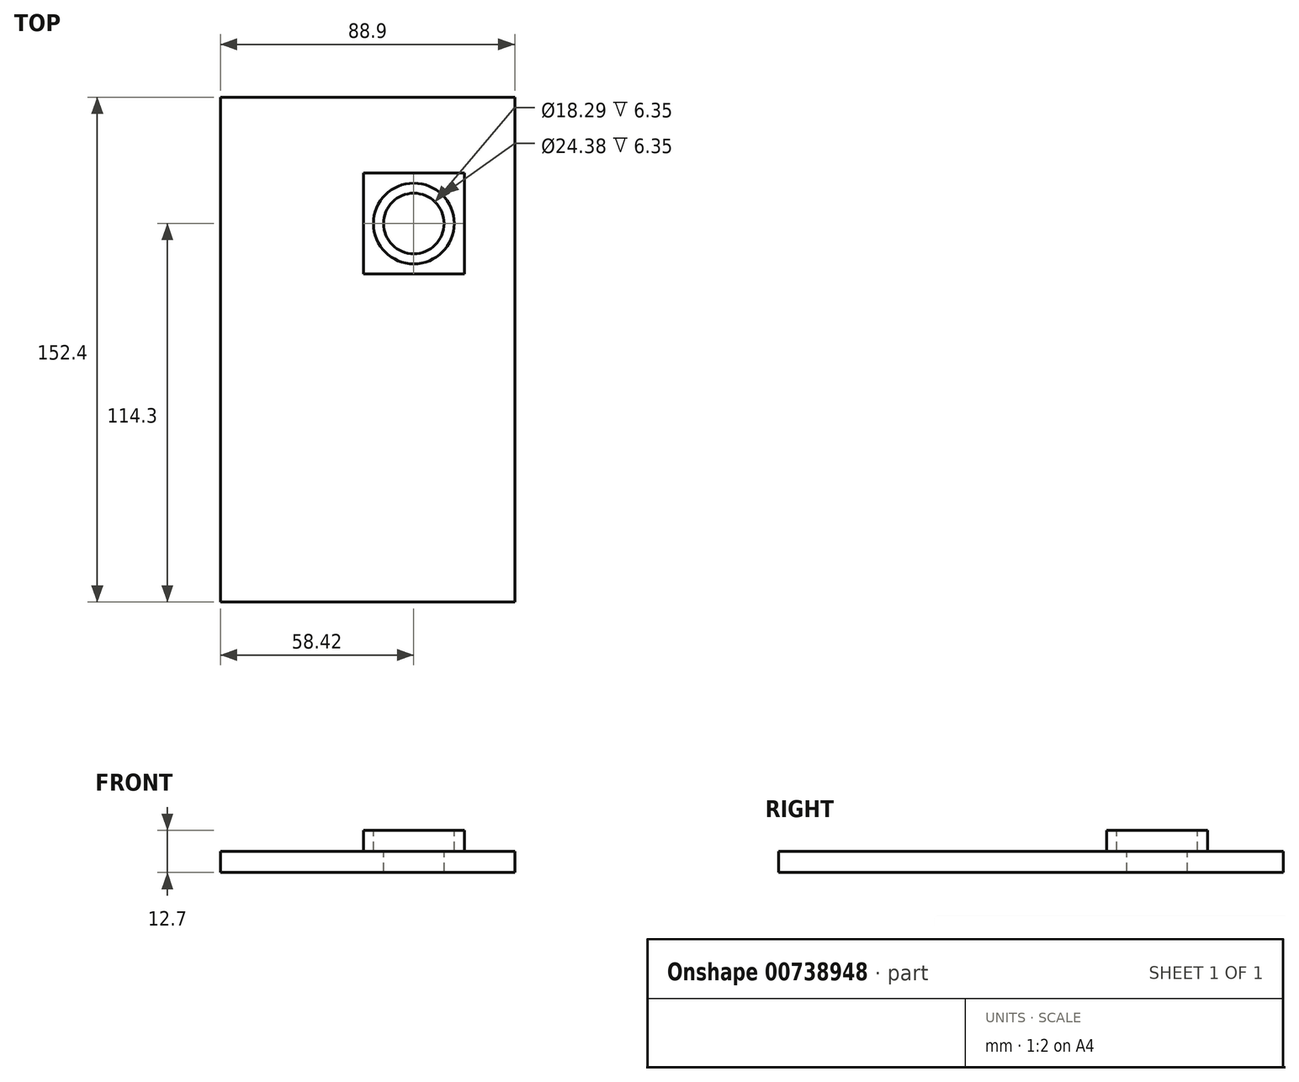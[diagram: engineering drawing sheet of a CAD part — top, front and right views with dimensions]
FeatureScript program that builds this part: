
annotation { "Feature Type Name" : "Feature", "Feature Type Description" : "" }
export const myFeature = defineFeature(function(context is Context, id is Id, definition is map)
    precondition{}
    {
        {
            var Q0;
            Q0=qCreatedBy(makeId("Top.planeOp"),FACE);
            var sketch = newSketch(context, id + "F0", { "sketchPlane" : qUnion([Q0])});
            skLineSegment(sketch, "E0.bottom", {"start": v(44.45, -76.2) * mm, "end": v(-44.45, -76.2) * mm});
            skLineSegment(sketch, "E0.top", {"start": v(44.45, 76.2) * mm, "end": v(-44.45, 76.2) * mm});
            skLineSegment(sketch, "E0.left", {"start": v(44.45, -76.2) * mm, "end": v(44.45, 76.2) * mm});
            skLineSegment(sketch, "E0.right", {"start": v(-44.45, -76.2) * mm, "end": v(-44.45, 76.2) * mm});
            skPoint(sketch, "E0.middle", {"position": v(0, 0) * mm});
            skPoint(sketch, "E1", {"position": v(13.97, 38.1) * mm});
            skLineSegment(sketch, "E2", {"start": v(13.97, 76.2) * mm, "end": v(13.97, 38.1) * mm});
            skLineSegment(sketch, "E3", {"start": v(44.45, 38.1) * mm, "end": v(13.97, 38.1) * mm});
            skLineSegment(sketch, "E4.bottom", {"start": v(29.2, 22.86) * mm, "end": v(-1.27, 22.86) * mm});
            skLineSegment(sketch, "E4.top", {"start": v(29.2, 53.34) * mm, "end": v(-1.27, 53.34) * mm});
            skLineSegment(sketch, "E4.left", {"start": v(29.2, 22.86) * mm, "end": v(29.2, 53.34) * mm});
            skLineSegment(sketch, "E4.right", {"start": v(-1.27, 22.86) * mm, "end": v(-1.27, 53.34) * mm});
            skSolve(sketch);
        }
        {
            var Q0;
            {var subQ1=sQuery(id+"F0.wireOp",EDGE,"E0.bottom");Q0=makeQuery(id+"F0.imprint","IMPRINT",FACE,{"disambiguationData":[TD([[makeQuery(id+"F0.imprint","IMPRINT",EDGE,{"derivedFrom":subQ1}),-1.0]])]});}
            var Q1;
            {var subQ1=sQuery(id+"F0.wireOp",EDGE,"E0.left");var subQ5=sQuery(id+"F0.wireOp",EDGE,"E0.top");var subQ6=makeQuery(id+"F0.imprint","INTERSECT",VERTEX,{"derivedFrom":[subQ5,subQ1]});Q1=makeQuery(id+"F0.imprint","IMPRINT",FACE,{"disambiguationData":[TD([[makeQuery(id+"F0.imprint","IMPRINT",EDGE,{"disambiguationData":[TD([[subQ6,-1.0]])],"derivedFrom":subQ5}),1.0]])]});}
            extrude(context, id + "F1", {"entities" : qUnion([Q0, Q1]), "depth" : 6.35 * mm, "offsetDistance" : 25.4 * mm});
        }
        {
            var Q0;
            {var subQ0=sQuery(id+"F0.wireOp",EDGE,"E4.bottom");Q0=makeQuery(id+"F0.imprint","IMPRINT",FACE,{"disambiguationData":[TD([[makeQuery(id+"F0.imprint","IMPRINT",EDGE,{"derivedFrom":subQ0}),-1.0]])]});}
            var Q1;
            {var subQ0=sQuery(id+"F0.wireOp",EDGE,"E3");var subQ1=sQuery(id+"F0.wireOp",EDGE,"E2");var subQ2=makeQuery(id+"F0.imprint","INTERSECT",VERTEX,{"derivedFrom":[subQ1,subQ0]});Q1=makeQuery(id+"F0.imprint","IMPRINT",FACE,{"disambiguationData":[TD([[makeQuery(id+"F0.imprint","IMPRINT",EDGE,{"disambiguationData":[TD([[subQ2,1.0]])],"derivedFrom":subQ1}),1.0]])]});}
            extrude(context, id + "F2", {"entities" : qUnion([Q0, Q1]), "operationType" : NewBodyOperationType.ADD, "depth" : 12.7 * mm, "offsetDistance" : 25.4 * mm});
        }
        {
            var Q0;
            Q0=makeQuery(id+"F2.opExtrude","CAP_FACE",FACE,{"disambiguationData":[OSD([sQuery(id+"F0.wireOp",EDGE,"E4.bottom"),sQuery(id+"F0.wireOp",EDGE,"E4.top"),sQuery(id+"F0.wireOp",EDGE,"E4.left"),sQuery(id+"F0.wireOp",EDGE,"E4.right")])],"isStart":false});
            var sketch = newSketch(context, id + "F3", { "sketchPlane" : qUnion([Q0])});
            skPoint(sketch, "E5", {"position": v(13.97, 38.1) * mm});
            skPoint(sketch, "E6", {"position": v(-26.97, 42.5) * mm});
            skLineSegment(sketch, "E7", {"start": v(13.97, 38.1) * mm, "end": v(13.97, 53.34) * mm});
            skLineSegment(sketch, "E8", {"start": v(13.97, 38.1) * mm, "end": v(29.2, 38.1) * mm});
            skSolve(sketch);
        }
        {
            var Q0;
            Q0=sQuery(id+"F3.wireOp",VERTEX,"E5");
            var Q1;
            Q1=makeQuery(id+"F1.opExtrude","SWEPT_BODY",BODY,{"disambiguationData":[OSD([sQuery(id+"F0.wireOp",EDGE,"E0.bottom"),sQuery(id+"F0.wireOp",EDGE,"E0.top"),sQuery(id+"F0.wireOp",EDGE,"E0.left"),sQuery(id+"F0.wireOp",EDGE,"E0.right"),sQuery(id+"F0.wireOp",EDGE,"E4.bottom"),sQuery(id+"F0.wireOp",EDGE,"E4.top"),sQuery(id+"F0.wireOp",EDGE,"E4.left"),sQuery(id+"F0.wireOp",EDGE,"E4.right")])]});
            hole(context, id + "F4", {"style" : HoleStyle.C_BORE, "endStyle" : HoleEndStyle.THROUGH, "holeDiameter" : 18.29 * mm, "cBoreDiameter" : 24.38 * mm, "cBoreDepth" : 6.35 * mm, "majorDiameter" : 6.35 * mm, "isTappedThrough" : true, "tappedDepth" : 12.7 * mm, "tapClearance" : 3, "locations" : qUnion([Q0]), "scope" : qUnion([Q1])});
        }
    });
